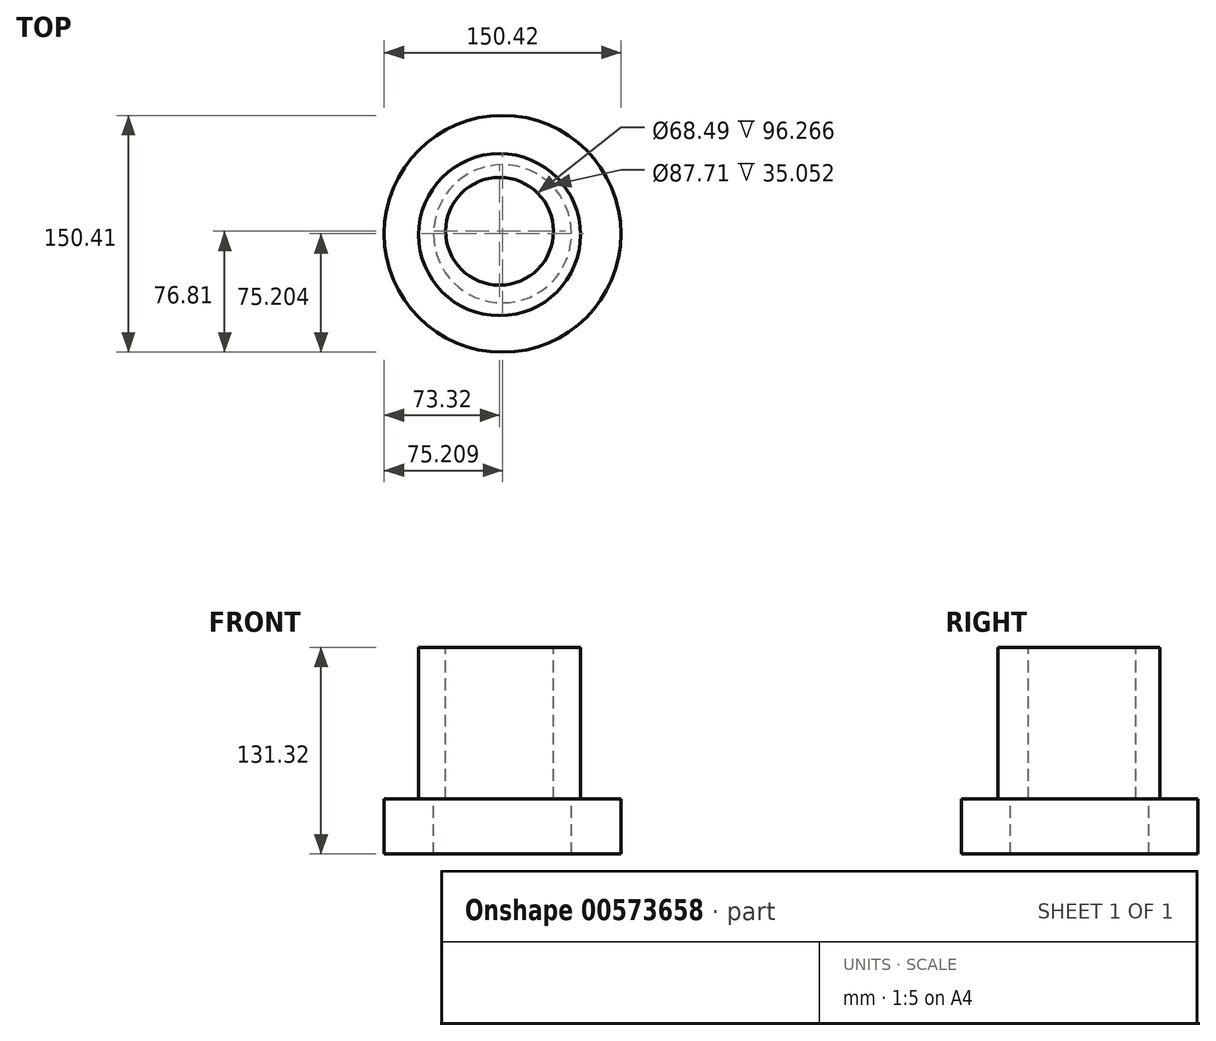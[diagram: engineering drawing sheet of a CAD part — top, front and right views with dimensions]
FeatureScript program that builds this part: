
annotation { "Feature Type Name" : "Feature", "Feature Type Description" : "" }
export const myFeature = defineFeature(function(context is Context, id is Id, definition is map)
    precondition{}
    {
        {
            var Q0;
            Q0=qCreatedBy(makeId("Top.planeOp"),FACE);
            var sketch = newSketch(context, id + "F0", { "sketchPlane" : qUnion([Q0])});
            skCircle(sketch, "E0", {"center": v(0, -2.17) * mm, "radius": 51.46 * mm});
            skCircle(sketch, "E1", {"center": v(0, 0) * mm, "radius": 34.24 * mm});
            skSolve(sketch);
        }
        {
            var Q0;
            Q0 = qSketchRegion(id + "F0", true);
            extrude(context, id + "F1", {"entities" : qUnion([Q0]), "oppositeDirection" : true, "depth" : 96.27 * mm, "offsetDistance" : 25.4 * mm});
        }
        {
            var Q0;
            Q0=makeQuery(id+"F1.opExtrude","CAP_FACE",FACE,{"disambiguationData":[OSD([sQuery(id+"F0.wireOp",EDGE,"E0"),sQuery(id+"F0.wireOp",EDGE,"E1")])],"isStart":false});
            var sketch = newSketch(context, id + "F2", { "sketchPlane" : qUnion([Q0])});
            skCircle(sketch, "E2", {"center": v(1.89, 1.6) * mm, "radius": 75.2 * mm});
            skCircle(sketch, "E3", {"center": v(1.89, 1.6) * mm, "radius": 43.85 * mm});
            skSolve(sketch);
        }
        {
            var Q0;
            Q0 = qSketchRegion(id + "F2", true);
            extrude(context, id + "F3", {"entities" : qUnion([Q0]), "operationType" : NewBodyOperationType.ADD, "depth" : 35.05 * mm, "offsetDistance" : 25.4 * mm});
        }
    });
